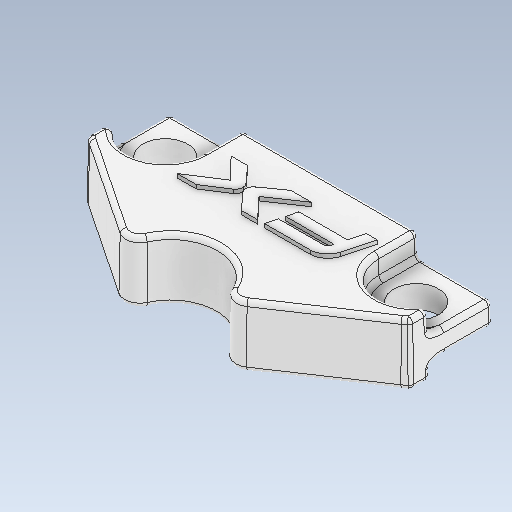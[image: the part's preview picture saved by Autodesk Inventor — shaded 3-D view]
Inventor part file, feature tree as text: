
AUTODESK INVENTOR PART (.ipt)
format: ipt  version: 2020 (Build 240168000, 168)  size: 483,328 bytes
history: native  units: in
note: dims shown in document units (in); Inventor stores cm internally (conversion verified against a paired STEP export)
features: fillet x1
ambient origin geometry x8: Origin, YZ Plane, XZ Plane, XY Plane, X Axis, Y Axis, Z Axis, Center Point
bodies: Solid1 (feature_tree)
feature tree (1):
  fillet  "Fillet3"  [1 undecoded]
note: 1 required parameter value undecoded (feature->parameter linkage not recoverable at this tier; creation-order binding heuristic only, values carry confidence <= 0.55)
